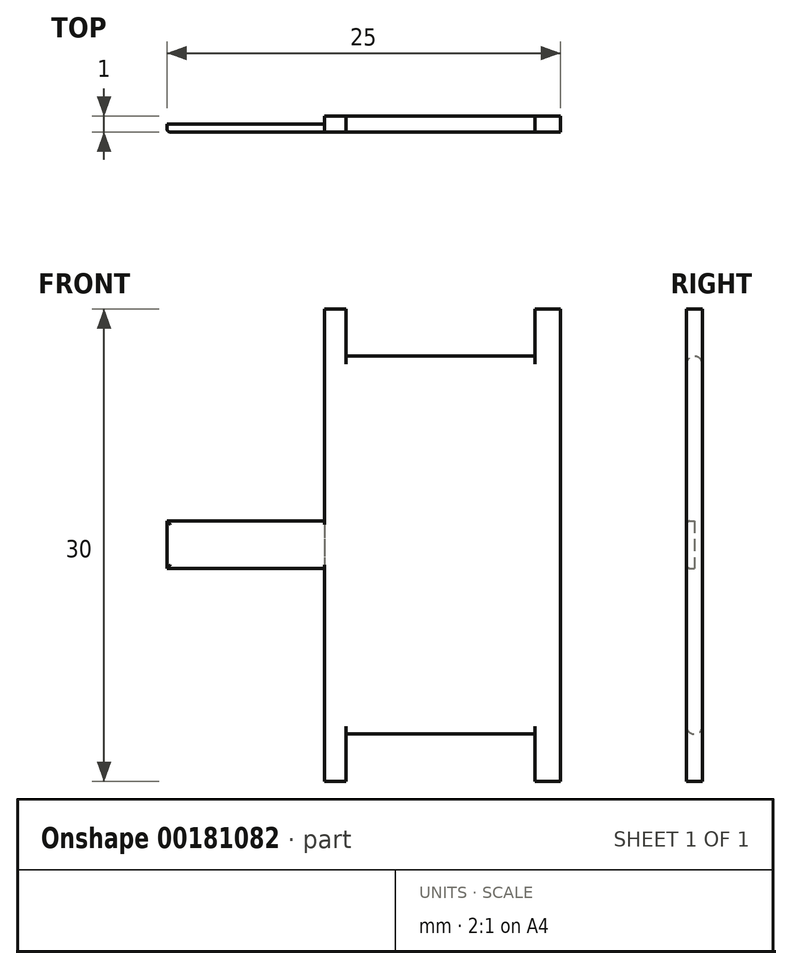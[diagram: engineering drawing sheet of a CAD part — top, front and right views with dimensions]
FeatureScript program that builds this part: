
annotation { "Feature Type Name" : "Feature", "Feature Type Description" : "" }
export const myFeature = defineFeature(function(context is Context, id is Id, definition is map)
    precondition{}
    {
        {
            var Q0;
            Q0=qCreatedBy(makeId("Front.planeOp"),FACE);
            var sketch = newSketch(context, id + "F0", { "sketchPlane" : qUnion([Q0])});
            skLineSegment(sketch, "E0.bottom", {"start": v(-7.5, 15) * mm, "end": v(7.5, 15) * mm});
            skLineSegment(sketch, "E0.top", {"start": v(-7.5, -15) * mm, "end": v(7.5, -15) * mm});
            skLineSegment(sketch, "E0.left", {"start": v(-7.5, 15) * mm, "end": v(-7.5, -15) * mm});
            skLineSegment(sketch, "E0.right", {"start": v(7.5, 15) * mm, "end": v(7.5, -15) * mm});
            skPoint(sketch, "E0.middle", {"position": v(0, 0) * mm});
            skLineSegment(sketch, "E1.bottom", {"start": v(-6.12, 15) * mm, "end": v(5.88, 15) * mm});
            skLineSegment(sketch, "E1.top", {"start": v(-6.12, 12) * mm, "end": v(5.88, 12) * mm});
            skLineSegment(sketch, "E1.left", {"start": v(-6.12, 15) * mm, "end": v(-6.12, 12) * mm});
            skLineSegment(sketch, "E1.right", {"start": v(5.88, 15) * mm, "end": v(5.88, 12) * mm});
            skLineSegment(sketch, "E2.bottom", {"start": v(-6.12, -15) * mm, "end": v(5.88, -15) * mm});
            skLineSegment(sketch, "E2.top", {"start": v(-6.12, -12) * mm, "end": v(5.88, -12) * mm});
            skLineSegment(sketch, "E2.left", {"start": v(-6.12, -15) * mm, "end": v(-6.12, -12) * mm});
            skLineSegment(sketch, "E2.right", {"start": v(5.88, -15) * mm, "end": v(5.88, -12) * mm});
            skLineSegment(sketch, "E3.bottom", {"start": v(-7.5, 1.53) * mm, "end": v(-17.5, 1.53) * mm});
            skLineSegment(sketch, "E3.top", {"start": v(-7.5, -1.47) * mm, "end": v(-17.5, -1.47) * mm});
            skLineSegment(sketch, "E3.left", {"start": v(-7.5, 1.53) * mm, "end": v(-7.5, -1.47) * mm});
            skLineSegment(sketch, "E3.right", {"start": v(-17.5, 1.53) * mm, "end": v(-17.5, -1.47) * mm});
            skSolve(sketch);
        }
        {
            var Q0;
            {var subQ4=sQuery(id+"F0.wireOp",EDGE,"E3.bottom");Q0=makeQuery(id+"F0.imprint","IMPRINT",FACE,{"disambiguationData":[TD([[makeQuery(id+"F0.imprint","IMPRINT",EDGE,{"derivedFrom":subQ4}),1.0]])]});}
            var Q1;
            {var subQ0=sQuery(id+"F0.wireOp",EDGE,"E0.right");Q1=makeQuery(id+"F0.imprint","IMPRINT",FACE,{"disambiguationData":[TD([[makeQuery(id+"F0.imprint","IMPRINT",EDGE,{"derivedFrom":subQ0}),-1.0]])]});}
            extrude(context, id + "F1", {"entities" : qUnion([Q0, Q1]), "depth" : 1 * mm});
        }
        {
            var Q0;
            Q0=makeQuery(id+"F0.imprint","IMPRINT",FACE,{"disambiguationData":[TD([[makeQuery(id+"F0.imprint","IMPRINT",EDGE,{"derivedFrom":sQuery(id+"F0.wireOp",EDGE,"E3.bottom")}),1.0]])]});
            extrude(context, id + "F2", {"entities" : qUnion([Q0]), "operationType" : NewBodyOperationType.REMOVE, "depth" : 0.5 * mm});
        }
        {
            var Q0;
            Q0=makeQuery(id+"F2.boolean.opBoolean","COPY",EDGE,{"derivedFrom":makeQuery(id+"F2.opExtrude","CAP_EDGE",EDGE,{"disambiguationData":[OSD([sQuery(id+"F0.wireOp",EDGE,"E3.top")])],"isStart":false})});
            var Q1;
            Q1=makeQuery(id+"F2.boolean.opBoolean","COPY",EDGE,{"derivedFrom":makeQuery(id+"F2.opExtrude","CAP_EDGE",EDGE,{"disambiguationData":[OSD([sQuery(id+"F0.wireOp",EDGE,"E3.bottom")])],"isStart":false})});
            var Q2;
            Q2=makeQuery(id+"F1.opExtrude","CAP_EDGE",EDGE,{"disambiguationData":[OSD([sQuery(id+"F0.wireOp",EDGE,"E3.top")])],"isStart":false});
            var Q3;
            Q3=makeQuery(id+"F1.opExtrude","CAP_EDGE",EDGE,{"disambiguationData":[OSD([sQuery(id+"F0.wireOp",EDGE,"E3.bottom")])],"isStart":false});
            var Q4;
            Q4=makeQuery(id+"F1.opExtrude","CAP_EDGE",EDGE,{"disambiguationData":[OSD([sQuery(id+"F0.wireOp",EDGE,"E3.right")])],"isStart":false});
            var Q5;
            Q5=makeQuery(id+"F2.boolean.opBoolean","COPY",EDGE,{"derivedFrom":makeQuery(id+"F2.opExtrude","CAP_EDGE",EDGE,{"disambiguationData":[OSD([sQuery(id+"F0.wireOp",EDGE,"E3.right")])],"isStart":false})});
            fillet(context, id + "F3", {"entities" : qUnion([Q0, Q1, Q2, Q3, Q4, Q5]), "radius" : 0.2 * mm, "tangentPropagation" : true, "allowEdgeOverflow" : false});
        }
        {
            var Q0;
            Q0=makeQuery(id+"F1.opExtrude","CAP_EDGE",EDGE,{"disambiguationData":[OSD([sQuery(id+"F0.wireOp",EDGE,"E2.top")])],"isStart":false});
            var Q1;
            Q1=makeQuery(id+"F1.opExtrude","CAP_EDGE",EDGE,{"disambiguationData":[OSD([sQuery(id+"F0.wireOp",EDGE,"E1.top")])],"isStart":false});
            var Q2;
            Q2=makeQuery(id+"F1.opExtrude","CAP_EDGE",EDGE,{"disambiguationData":[OSD([sQuery(id+"F0.wireOp",EDGE,"E2.top")])],"isStart":true});
            var Q3;
            Q3=makeQuery(id+"F1.opExtrude","CAP_EDGE",EDGE,{"disambiguationData":[OSD([sQuery(id+"F0.wireOp",EDGE,"E1.top")])],"isStart":true});
            fillet(context, id + "F4", {"entities" : qUnion([Q0, Q1, Q2, Q3]), "radius" : 0.5 * mm, "tangentPropagation" : true, "allowEdgeOverflow" : false});
        }
    });
